FCSTD DOCUMENT  (FreeCAD 0.18.3R)
Label: top_advanced
License: All rights reserved
LicenseURL: http://en.wikipedia.org/wiki/All_rights_reserved
objects: PartDesign::Body×2, Sketcher::SketchObject×1
note: 3 computed .brp shape members not serialized (recipe doc carries the construction recipe); baked Part::Feature solids carry a one-line shape summary decoded from their .brp

FEATURE [PartDesign::Body] Body
  Origin = -> Origin
FEATURE [Sketcher::SketchObject] Sketch
  MapMode = 5
  Placement = pos=(0,0,0) rot=(1,0,0;1.5708rad)
  Support = -> [XZ_Plane001]
  sketch-geometry (7):
    g0: Circle [constr] CenterX=0 CenterY=11.8042 CenterZ=0 NormalX=0 NormalY=0 NormalZ=1 AngleXU=0 Radius=3
    g1: Circle [constr] CenterX=19.3556 CenterY=10.2691 CenterZ=0 NormalX=0 NormalY=0 NormalZ=1 AngleXU=0 Radius=3
    g2: Circle [constr] CenterX=27 CenterY=3 CenterZ=0 NormalX=0 NormalY=0 NormalZ=1 AngleXU=0 Radius=3
    g3: BSplineCurve PolesCount=3 KnotsCount=2 Degree=2 IsPeriodic=0
    g4: GeomPoint [constr] X=0 Y=11.8042 Z=0
    g5: GeomPoint [constr] X=27 Y=3 Z=0
    g6: LineSegment StartX=27 StartY=3 StartZ=0 EndX=27 EndY=0 EndZ=0
  constraints (14):
    c: PointOnObject(g3,g-2)
    c: Radius(g0) = 3
    c: Equal(g0,g1)
    c: Equal(g0,g2)
    c: InternalAlignment(g0,g3)
    c: InternalAlignment(g1,g3)
    c: InternalAlignment(g2,g3)
    c: InternalAlignment(g4,g3)
    c: InternalAlignment(g5,g3)
    c: Coincident(g6,g3)
    c: PointOnObject(g6,g-1)
    c: Vertical(g6)
    c: DistanceX(g-1,g6) = 27
    c: DistanceY(g6,g6) = 3
FEATURE [PartDesign::Body] Body001
  Group = -> [Sketch]
  Origin = -> Origin001
